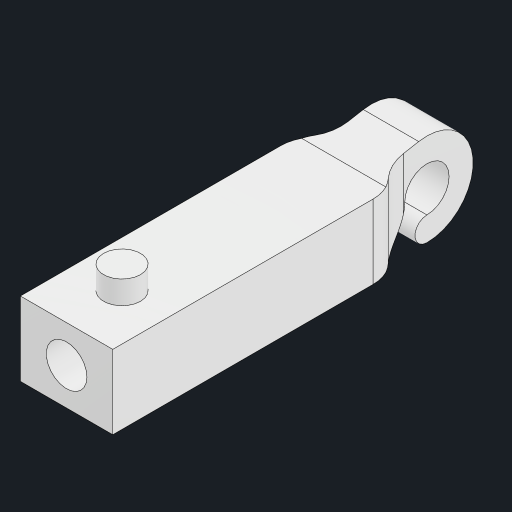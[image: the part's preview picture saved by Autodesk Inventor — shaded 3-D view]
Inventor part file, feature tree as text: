
AUTODESK INVENTOR PART (.ipt)
format: ipt  version: 2023 (Build 270158000, 158)  size: 162,816 bytes
history: native  units: mm
features: sketch x5, extrude x3, hole x2, other x1, fillet x1
ambient origin geometry x8: Origin, YZ Plane, XZ Plane, XY Plane, X Axis, Y Axis, Z Axis, Center Point
bodies: Body1 (feature_tree)
feature tree (12):
  other  "ソリッド1"
  extrude  "押し出し1"  Depth=5.0mm
  extrude  "押し出し2"  Depth=4.0mm TaperAngle=0.0deg
  hole  "加工用"  [1 undecoded]
  extrude  "押し出し4"  Depth=6.5mm TaperAngle=0.0deg
  fillet  "フィレット1"  Radius=15.0mm
  hole  "穴3"  [1 undecoded]
  sketch  "スケッチ1"
  sketch  "スケッチ2"
  sketch  "スケッチ5"
  sketch  "スケッチ6"
  sketch  "スケッチ8"
note: 2 required parameter values undecoded (feature->parameter linkage not recoverable at this tier; creation-order binding heuristic only, values carry confidence <= 0.55)
